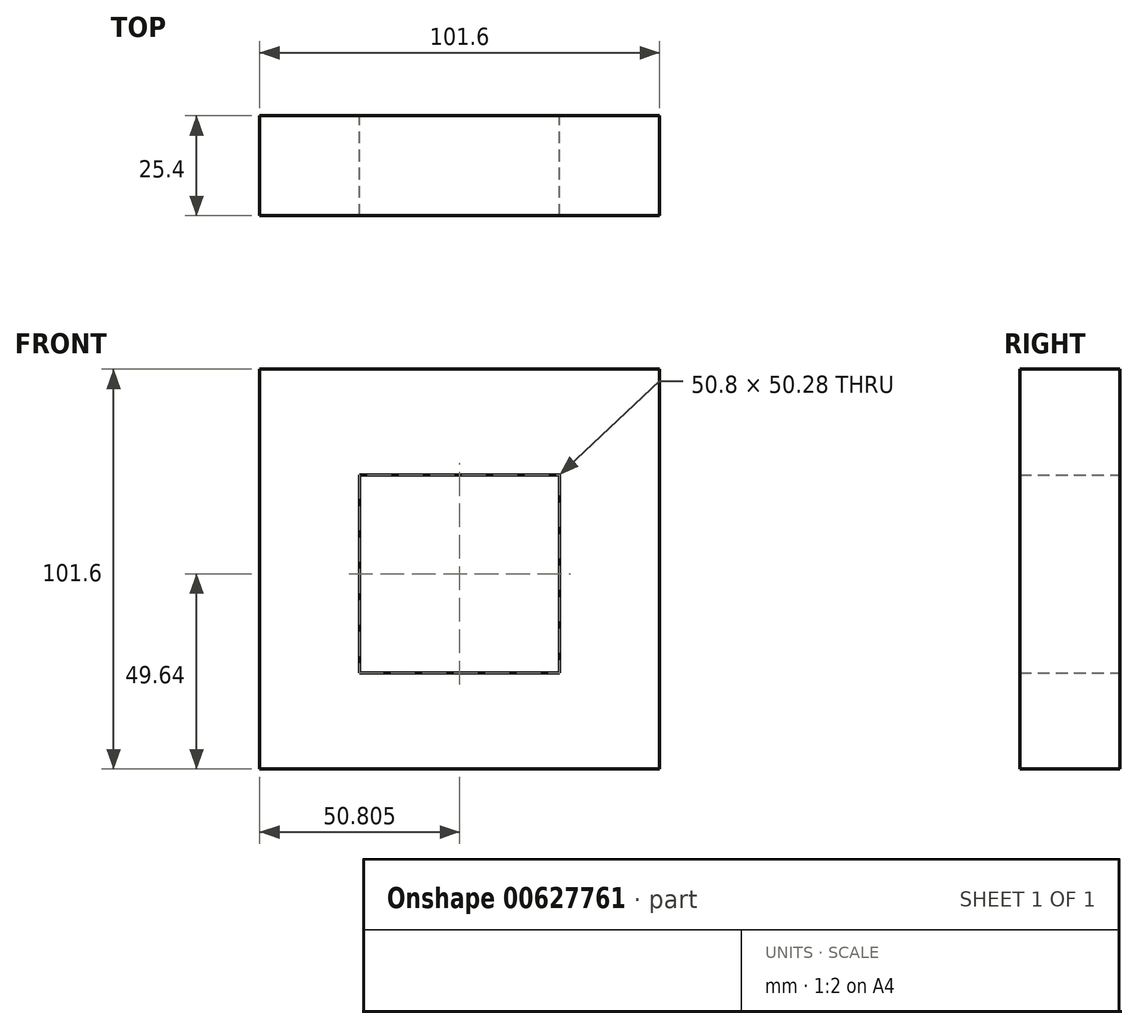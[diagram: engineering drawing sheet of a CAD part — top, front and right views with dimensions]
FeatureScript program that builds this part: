
annotation { "Feature Type Name" : "Feature", "Feature Type Description" : "" }
export const myFeature = defineFeature(function(context is Context, id is Id, definition is map)
    precondition{}
    {
        {
            var Q0;
            Q0=qCreatedBy(makeId("Front.planeOp"),FACE);
            var sketch = newSketch(context, id + "F0", { "sketchPlane" : qUnion([Q0])});
            skLineSegment(sketch, "E0", {"start": v(-53.1, 49.3) * mm, "end": v(-53.1, -52.3) * mm});
            skLineSegment(sketch, "E1", {"start": v(-53.1, -52.3) * mm, "end": v(48.5, -52.3) * mm});
            skLineSegment(sketch, "E2", {"start": v(48.5, -52.3) * mm, "end": v(48.5, 49.3) * mm});
            skLineSegment(sketch, "E3", {"start": v(48.5, 49.3) * mm, "end": v(-53.1, 49.3) * mm});
            skLineSegment(sketch, "E4", {"start": v(-27.7, 22.5) * mm, "end": v(23.1, 22.5) * mm});
            skLineSegment(sketch, "E5", {"start": v(23.1, 22.5) * mm, "end": v(23.1, -27.8) * mm});
            skLineSegment(sketch, "E6", {"start": v(-27.7, 22.5) * mm, "end": v(-27.7, -27.8) * mm});
            skLineSegment(sketch, "E7", {"start": v(-27.7, -27.8) * mm, "end": v(23.1, -27.8) * mm});
            skSolve(sketch);
        }
        {
            var Q0;
            Q0 = qSketchRegion(id + "F0", true);
            extrude(context, id + "F1", {"entities" : qUnion([Q0]), "depth" : 25.4 * mm, "offsetDistance" : 25.4 * mm});
        }
    });
